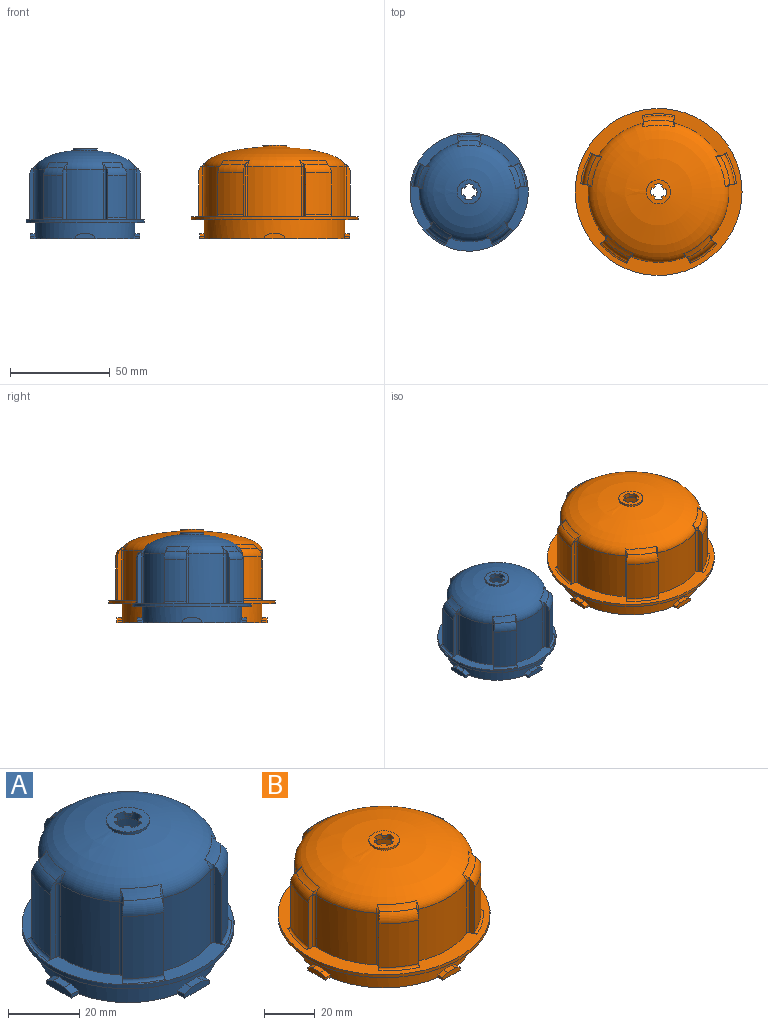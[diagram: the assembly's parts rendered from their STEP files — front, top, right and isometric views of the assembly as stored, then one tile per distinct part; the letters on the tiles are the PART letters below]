
ASSEMBLY  parts=2 mates=1
PART A: 108 faces, bbox 81.5x78.8x51.9 mm
  f0: revolved ~47x47mm, area 2029.6mm2, adj f4,f90
  f1: revolved ~50x50mm, area 2139.5mm2, adj f33,f37,f41,f45,f49,f52,f53,f54
  f2: plane 59.35x59.35mm, normal (0,0,1), area 574.8mm2, adj f30,f32,f33,f34,f36,f37,f38,f40
  f3: cylinder r=25mm len=50mm, axis (0,0,-1), area 1174.5mm2, adj f5,f7,f8,f9,f11,f12,f13,f15
  f4: cylinder r=23.5mm len=47mm, axis (0,0,-1), area 5079.3mm2, adj f0,f5
  f5: plane 54.75x54.75mm, normal (0,0,-1), area 328mm2, adj f3,f4,f6,f7,f8,f10,f11,f12
  f6: plane 9.8x2.4mm, normal (0,1,0), area 20.4mm2, adj f5,f7,f8,f9,f23,f27
  f7: plane 2.86x1.2mm, normal (-1,0,0), area 3.4mm2, adj f3,f5,f6,f23
  f8: plane 2.86x1.2mm, normal (1,0,0), area 3.4mm2, adj f3,f5,f6,f27
  f9: plane 4.6x2.48mm, normal (0,0,1), area 11.1mm2, adj f3,f6,f23,f27
  f10: plane 9.8x2.4mm, normal (1,0,0), area 20.4mm2, adj f5,f11,f12,f13,f24,f29
  f11: plane 2.86x1.2mm, normal (0,1,0), area 3.4mm2, adj f3,f5,f10,f24
  f12: plane 2.86x1.2mm, normal (0,-1,0), area 3.4mm2, adj f3,f5,f10,f29
  f13: plane 4.6x2.48mm, normal (0,0,1), area 11.1mm2, adj f3,f10,f24,f29
  f14: plane 9.8x2.4mm, normal (0,-1,0), area 20.4mm2, adj f5,f15,f16,f17,f25,f28
  f15: plane 2.86x1.2mm, normal (1,0,0), area 3.4mm2, adj f3,f5,f14,f25
  f16: plane 2.86x1.2mm, normal (-1,0,0), area 3.4mm2, adj f3,f5,f14,f28
  f17: plane 4.6x2.48mm, normal (0,0,1), area 11.1mm2, adj f3,f14,f25,f28
  f18: plane 9.8x2.4mm, normal (-1,0,0), area 20.4mm2, adj f5,f19,f20,f21,f22,f26
  f19: plane 2.86x1.2mm, normal (0,-1,0), area 3.4mm2, adj f3,f5,f18,f22
  f20: plane 2.86x1.2mm, normal (0,1,0), area 3.4mm2, adj f3,f5,f18,f26
  f21: plane 4.6x2.48mm, normal (0,0,1), area 11.1mm2, adj f3,f18,f22,f26
  f22: plane 2.86x2.6mm, normal (0,-0.42,0.91), area 7.6mm2, adj f3,f18,f19,f21
  f23: plane 2.86x2.6mm, normal (-0.42,0,0.91), area 7.6mm2, adj f3,f6,f7,f9
  f24: plane 2.86x2.6mm, normal (0,0.42,0.91), area 7.6mm2, adj f3,f10,f11,f13
  f25: plane 2.86x2.6mm, normal (0.42,0,0.91), area 7.6mm2, adj f3,f14,f15,f17
  f26: plane 2.86x2.6mm, normal (0,0.42,0.91), area 7.6mm2, adj f3,f18,f20,f21
  f27: plane 2.86x2.6mm, normal (0.42,0,0.91), area 7.6mm2, adj f3,f6,f8,f9
  f28: plane 2.86x2.6mm, normal (-0.42,0,0.91), area 7.6mm2, adj f3,f14,f16,f17
  f29: plane 2.86x2.6mm, normal (0,-0.42,0.91), area 7.6mm2, adj f3,f10,f12,f13
  f30: cylinder r=29.68mm len=59.35mm, axis (0,0,-1), area 261mm2, adj f2,f31
  f31: plane 59.35x59.35mm, normal (0,0,-1), area 803mm2, adj f3,f30
  f32: plane 26.45x3.16mm, normal (-0.98,-0.21,0), area 50.9mm2, adj f2,f51,f55,f61,f64,f65,f86
  f33: cylinder r=25mm len=25mm, axis (0,0,-1), area 475.5mm2, adj f1,f2,f64,f66
  f34: plane 26.45x2.8mm, normal (0.5,0.87,0), area 50.9mm2, adj f2,f35,f56,f60,f66,f67,f85
  f35: cylinder r=28mm len=21.27mm, axis (0,0,-1), area 249.5mm2, adj f34,f36,f60,f85
  f36: plane 26.45x3.21mm, normal (-0.1,-0.99,0), area 50.9mm2, adj f2,f35,f56,f60,f68,f69,f85
  f37: cylinder r=25mm len=25mm, axis (0,0,-1), area 475.5mm2, adj f1,f2,f68,f70
  f38: plane 26.45x2.4mm, normal (-0.67,0.74,0), area 50.9mm2, adj f2,f39,f52,f59,f70,f71,f84
  f39: cylinder r=28mm len=21.27mm, axis (0,0,-1), area 249.5mm2, adj f38,f40,f59,f84
  f40: plane 26.45x2.95mm, normal (0.91,-0.41,0), area 50.9mm2, adj f2,f39,f52,f59,f72,f73,f84
  f41: cylinder r=25mm len=25mm, axis (0,0,-1), area 475.5mm2, adj f1,f2,f72,f74
  f42: plane 26.45x2.95mm, normal (-0.91,-0.41,0), area 50.9mm2, adj f2,f43,f53,f58,f74,f75,f83
  f43: cylinder r=28mm len=21.27mm, axis (0,0,-1), area 249.5mm2, adj f42,f44,f58,f83
  f44: plane 26.45x2.4mm, normal (0.67,0.74,0), area 50.9mm2, adj f2,f43,f53,f58,f76,f77,f83
  f45: cylinder r=25mm len=25mm, axis (0,0,-1), area 475.5mm2, adj f1,f2,f76,f78
  f46: plane 26.45x3.21mm, normal (0.1,-0.99,0), area 50.9mm2, adj f2,f47,f54,f57,f78,f79,f82
  f47: cylinder r=28mm len=21.27mm, axis (0,0,-1), area 249.5mm2, adj f46,f48,f57,f82
  f48: plane 26.45x2.8mm, normal (-0.5,0.87,0), area 50.9mm2, adj f2,f47,f54,f57,f80,f81,f82
  f49: cylinder r=25mm len=25mm, axis (0,0,-1), area 475.5mm2, adj f1,f2,f62,f80
  f50: plane 26.45x3.16mm, normal (0.98,-0.21,0), area 50.9mm2, adj f2,f51,f55,f61,f62,f63,f86
  f51: cylinder r=28mm len=21.27mm, axis (0,0,-1), area 249.5mm2, adj f32,f50,f61,f86
  f52: torus R=37.73mm, axis (0,0,-1), area 38.3mm2, adj f1,f38,f40,f59,f71,f73
  f53: torus R=37.73mm, axis (0,0,-1), area 38.3mm2, adj f1,f42,f44,f58,f75,f77
  f54: torus R=37.73mm, axis (0,0,-1), area 38.3mm2, adj f1,f46,f48,f57,f79,f81
  f55: torus R=37.73mm, axis (0,0,-1), area 38.3mm2, adj f1,f32,f50,f61,f63,f65
  f56: torus R=37.73mm, axis (0,0,-1), area 38.3mm2, adj f1,f34,f36,f60,f67,f69
  f57: torus R=23mm, axis (0,0,1), area 53.8mm2, adj f46,f47,f48,f54
  f58: torus R=23mm, axis (0,0,1), area 53.8mm2, adj f42,f43,f44,f53
  f59: torus R=23mm, axis (0,0,1), area 53.8mm2, adj f38,f39,f40,f52
  f60: torus R=23mm, axis (0,0,1), area 53.8mm2, adj f34,f35,f36,f56
  f61: torus R=23mm, axis (0,0,1), area 53.8mm2, adj f32,f50,f51,f55
  f62: cylinder r=1mm len=25mm, axis (0,0,-1), area 38.3mm2, adj f2,f49,f50,f63
  f63: bspline ~6.12x3.69mm, area 4.2mm2, adj f1,f50,f55,f62
  f64: cylinder r=1mm len=25mm, axis (0,0,-1), area 38.3mm2, adj f2,f32,f33,f65
  f65: bspline ~6.12x3.69mm, area 4.2mm2, adj f1,f32,f55,f64
  f66: cylinder r=1mm len=25mm, axis (0,0,-1), area 38.3mm2, adj f2,f33,f34,f67
  f67: bspline ~6.12x3.57mm, area 4.2mm2, adj f1,f34,f56,f66
  f68: cylinder r=1mm len=25mm, axis (0,0,-1), area 38.3mm2, adj f2,f36,f37,f69
  f69: bspline ~6.12x3.53mm, area 4.2mm2, adj f1,f36,f56,f68
  f70: cylinder r=1mm len=25mm, axis (0,0,-1), area 38.3mm2, adj f2,f37,f38,f71
  f71: bspline ~6.12x3.11mm, area 4.2mm2, adj f1,f38,f52,f70
  f72: cylinder r=1mm len=25mm, axis (0,0,-1), area 38.3mm2, adj f2,f40,f41,f73
  f73: bspline ~6.12x3.24mm, area 4.2mm2, adj f1,f40,f52,f72
  f74: cylinder r=1mm len=25mm, axis (0,0,-1), area 38.3mm2, adj f2,f41,f42,f75
  f75: bspline ~6.12x3.24mm, area 4.2mm2, adj f1,f42,f53,f74
  f76: cylinder r=1mm len=25mm, axis (0,0,-1), area 38.3mm2, adj f2,f44,f45,f77
  f77: bspline ~6.12x3.11mm, area 4.2mm2, adj f1,f44,f53,f76
  f78: cylinder r=1mm len=25mm, axis (0,0,-1), area 38.3mm2, adj f2,f45,f46,f79
  f79: bspline ~6.12x3.53mm, area 4.2mm2, adj f1,f46,f54,f78
  f80: cylinder r=1mm len=25mm, axis (0,0,-1), area 38.3mm2, adj f2,f48,f49,f81
  f81: bspline ~6.12x3.57mm, area 4.2mm2, adj f1,f48,f54,f80
  f82: torus R=29mm, axis (0,0,1), area 18.7mm2, adj f2,f46,f47,f48
  f83: torus R=29mm, axis (0,0,1), area 18.7mm2, adj f2,f42,f43,f44
  f84: torus R=29mm, axis (0,0,1), area 18.7mm2, adj f2,f38,f39,f40
  f85: torus R=29mm, axis (0,0,1), area 18.7mm2, adj f2,f34,f35,f36
  f86: torus R=29mm, axis (0,0,1), area 18.7mm2, adj f2,f32,f50,f51
  f87: plane 12x12mm, normal (0,0,1), area 70.2mm2, adj f88,f89,f92,f93,f94,f96,f97,f98
  f88: cylinder r=6mm len=12mm, axis (0,0,-1), area 33.7mm2, adj f1,f87
  f89: cylinder r=4mm len=8mm, axis (0,0,-1), area 54.5mm2, adj f87,f91,f92,f94,f95,f96,f98,f99
  f90: cylinder r=6mm len=12mm, axis (0,0,-1), area 4.4mm2, adj f0,f91
  f91: plane 12x12mm, normal (0,0,-1), area 62.8mm2, adj f89,f90
  f92: plane 1x0.85mm, normal (-0.53,-0.85,0), area 1mm2, adj f87,f89,f93,f95
  f93: cylinder r=3mm len=1.14mm, axis (0,0,1), area 1.6mm2, adj f87,f92,f94,f95
  f94: plane 1x0.89mm, normal (0.89,0.47,0), area 1mm2, adj f87,f89,f93,f95
  f95: plane 1.99x1.94mm, normal (0,0,-1), area 1.8mm2, adj f89,f92,f93,f94
  f96: plane 1x0.85mm, normal (0.85,-0.53,0), area 1mm2, adj f87,f89,f97,f99
  f97: cylinder r=3mm len=1.14mm, axis (0,0,1), area 1.6mm2, adj f87,f96,f98,f99
  f98: plane 1x0.89mm, normal (-0.47,0.89,0), area 1mm2, adj f87,f89,f97,f99
  f99: plane 1.99x1.94mm, normal (0,0,-1), area 1.8mm2, adj f89,f96,f97,f98
  f100: plane 1x0.85mm, normal (0.53,0.85,0), area 1mm2, adj f87,f89,f101,f103
  f101: cylinder r=3mm len=1.14mm, axis (0,0,1), area 1.6mm2, adj f87,f100,f102,f103
  f102: plane 1x0.89mm, normal (-0.89,-0.47,0), area 1mm2, adj f87,f89,f101,f103
  f103: plane 1.99x1.94mm, normal (0,0,-1), area 1.8mm2, adj f89,f100,f101,f102
  f104: plane 1x0.85mm, normal (-0.85,0.53,0), area 1mm2, adj f87,f89,f105,f107
  f105: cylinder r=3mm len=1.14mm, axis (0,0,1), area 1.6mm2, adj f87,f104,f106,f107
  f106: plane 1x0.89mm, normal (0.47,-0.89,0), area 1mm2, adj f87,f89,f105,f107
  f107: plane 1.99x1.94mm, normal (0,0,-1), area 1.8mm2, adj f89,f104,f105,f106
PART B: 108 faces, bbox 100.9x97.4x46.7 mm
  f0: revolved ~67.5x67.5mm, area 3947.5mm2, adj f4,f90
  f1: revolved ~70.5x70.5mm, area 4124.4mm2, adj f33,f37,f41,f45,f49,f52,f53,f54
  f2: plane 83.68x83.68mm, normal (0,0,1), area 1282.3mm2, adj f30,f32,f33,f34,f36,f37,f38,f40
  f3: cylinder r=35.25mm len=70.5mm, axis (0,0,-1), area 2035.9mm2, adj f5,f7,f8,f9,f11,f12,f13,f15
  f4: cylinder r=33.75mm len=67.5mm, axis (0,0,-1), area 7625.9mm2, adj f0,f5
  f5: plane 75.25x75.25mm, normal (0,0,-1), area 422.7mm2, adj f3,f4,f6,f7,f8,f10,f11,f12
  f6: plane 9.8x2.4mm, normal (0,1,0), area 20.4mm2, adj f5,f7,f8,f9,f23,f27
  f7: plane 2.72x1.2mm, normal (-1,0,0), area 3.3mm2, adj f3,f5,f6,f23
  f8: plane 2.72x1.2mm, normal (1,0,0), area 3.3mm2, adj f3,f5,f6,f27
  f9: plane 4.6x2.45mm, normal (0,0,1), area 11mm2, adj f3,f6,f23,f27
  f10: plane 9.8x2.4mm, normal (1,0,0), area 20.4mm2, adj f5,f11,f12,f13,f24,f29
  f11: plane 2.72x1.2mm, normal (0,1,0), area 3.3mm2, adj f3,f5,f10,f24
  f12: plane 2.72x1.2mm, normal (0,-1,0), area 3.3mm2, adj f3,f5,f10,f29
  f13: plane 4.6x2.45mm, normal (0,0,1), area 11mm2, adj f3,f10,f24,f29
  f14: plane 9.8x2.4mm, normal (0,-1,0), area 20.4mm2, adj f5,f15,f16,f17,f25,f28
  f15: plane 2.72x1.2mm, normal (1,0,0), area 3.3mm2, adj f3,f5,f14,f25
  f16: plane 2.72x1.2mm, normal (-1,0,0), area 3.3mm2, adj f3,f5,f14,f28
  f17: plane 4.6x2.45mm, normal (0,0,1), area 11mm2, adj f3,f14,f25,f28
  f18: plane 9.8x2.4mm, normal (-1,0,0), area 20.4mm2, adj f5,f19,f20,f21,f22,f26
  f19: plane 2.72x1.2mm, normal (0,-1,0), area 3.3mm2, adj f3,f5,f18,f22
  f20: plane 2.72x1.2mm, normal (0,1,0), area 3.3mm2, adj f3,f5,f18,f26
  f21: plane 4.6x2.45mm, normal (0,0,1), area 11mm2, adj f3,f18,f22,f26
  f22: plane 2.72x2.6mm, normal (0,-0.42,0.91), area 7.4mm2, adj f3,f18,f19,f21
  f23: plane 2.72x2.6mm, normal (-0.42,0,0.91), area 7.4mm2, adj f3,f6,f7,f9
  f24: plane 2.72x2.6mm, normal (0,0.42,0.91), area 7.4mm2, adj f3,f10,f11,f13
  f25: plane 2.72x2.6mm, normal (0.42,0,0.91), area 7.4mm2, adj f3,f14,f15,f17
  f26: plane 2.72x2.6mm, normal (0,0.42,0.91), area 7.4mm2, adj f3,f18,f20,f21
  f27: plane 2.72x2.6mm, normal (0.42,0,0.91), area 7.4mm2, adj f3,f6,f8,f9
  f28: plane 2.72x2.6mm, normal (-0.42,0,0.91), area 7.4mm2, adj f3,f14,f16,f17
  f29: plane 2.72x2.6mm, normal (0,-0.42,0.91), area 7.4mm2, adj f3,f10,f12,f13
  f30: cylinder r=41.84mm len=83.68mm, axis (0,0,-1), area 368.1mm2, adj f2,f31
  f31: plane 83.68x83.68mm, normal (0,0,-1), area 1596.5mm2, adj f3,f30
  f32: plane 26.21x3.14mm, normal (-0.98,-0.21,0), area 50.3mm2, adj f2,f51,f61,f64,f65,f86
  f33: cylinder r=35.25mm len=25mm, axis (0,0,-1), area 689.6mm2, adj f1,f2,f64,f66
  f34: plane 26.21x2.78mm, normal (0.5,0.87,0), area 50.3mm2, adj f2,f35,f60,f66,f67,f85
  f35: cylinder r=38.25mm len=21.06mm, axis (0,0,-1), area 337.4mm2, adj f34,f36,f60,f85
  f36: plane 26.21x3.19mm, normal (-0.1,-0.99,0), area 50.3mm2, adj f2,f35,f60,f68,f69,f85
  f37: cylinder r=35.25mm len=25.57mm, axis (0,0,-1), area 689.6mm2, adj f1,f2,f68,f70
  f38: plane 26.21x2.38mm, normal (-0.67,0.74,0), area 50.3mm2, adj f2,f39,f59,f70,f71,f84
  f39: cylinder r=38.25mm len=21.06mm, axis (0,0,-1), area 337.4mm2, adj f38,f40,f59,f84
  f40: plane 26.21x2.93mm, normal (0.91,-0.41,0), area 50.3mm2, adj f2,f39,f59,f72,f73,f84
  f41: cylinder r=35.25mm len=26.89mm, axis (0,0,-1), area 689.6mm2, adj f1,f2,f72,f74
  f42: plane 26.21x2.93mm, normal (-0.91,-0.41,0), area 50.3mm2, adj f2,f43,f58,f74,f75,f83
  f43: cylinder r=38.25mm len=21.06mm, axis (0,0,-1), area 337.4mm2, adj f42,f44,f58,f83
  f44: plane 26.21x2.38mm, normal (0.67,0.74,0), area 50.3mm2, adj f2,f43,f58,f76,f77,f83
  f45: cylinder r=35.25mm len=25.57mm, axis (0,0,-1), area 689.6mm2, adj f1,f2,f76,f78
  f46: plane 26.21x3.19mm, normal (0.1,-0.99,0), area 50.3mm2, adj f2,f47,f57,f78,f79,f82
  f47: cylinder r=38.25mm len=21.06mm, axis (0,0,-1), area 337.4mm2, adj f46,f48,f57,f82
  f48: plane 26.21x2.78mm, normal (-0.5,0.87,0), area 50.3mm2, adj f2,f47,f57,f80,f81,f82
  f49: cylinder r=35.25mm len=25mm, axis (0,0,-1), area 689.6mm2, adj f1,f2,f62,f80
  f50: plane 26.21x3.14mm, normal (0.98,-0.21,0), area 50.3mm2, adj f2,f51,f61,f62,f63,f86
  f51: cylinder r=38.25mm len=21.06mm, axis (0,0,-1), area 337.4mm2, adj f32,f50,f61,f86
  f52: torus R=46.72mm, axis (0,0,-1), area 46.9mm2, adj f1,f59,f71,f73
  f53: torus R=46.72mm, axis (0,0,-1), area 46.9mm2, adj f1,f58,f75,f77
  f54: torus R=46.72mm, axis (0,0,-1), area 46.9mm2, adj f1,f57,f79,f81
  f55: torus R=46.72mm, axis (0,0,-1), area 46.9mm2, adj f1,f61,f63,f65
  f56: torus R=46.72mm, axis (0,0,-1), area 46.9mm2, adj f1,f60,f67,f69
  f57: torus R=33.25mm, axis (0,0,1), area 78.6mm2, adj f46,f47,f48,f54,f79,f81
  f58: torus R=33.25mm, axis (0,0,1), area 78.6mm2, adj f42,f43,f44,f53,f75,f77
  f59: torus R=33.25mm, axis (0,0,1), area 78.6mm2, adj f38,f39,f40,f52,f71,f73
  f60: torus R=33.25mm, axis (0,0,1), area 78.6mm2, adj f34,f35,f36,f56,f67,f69
  f61: torus R=33.25mm, axis (0,0,1), area 78.6mm2, adj f32,f50,f51,f55,f63,f65
  f62: cylinder r=1mm len=25mm, axis (0,0,-1), area 38.6mm2, adj f2,f49,f50,f63
  f63: bspline ~4.73x3.44mm, area 3.4mm2, adj f1,f50,f55,f61,f62
  f64: cylinder r=1mm len=25mm, axis (0,0,-1), area 38.6mm2, adj f2,f32,f33,f65
  f65: bspline ~4.73x3.44mm, area 3.4mm2, adj f1,f32,f55,f61,f64
  f66: cylinder r=1mm len=25mm, axis (0,0,-1), area 38.6mm2, adj f2,f33,f34,f67
  f67: bspline ~4.73x3.36mm, area 3.4mm2, adj f1,f34,f56,f60,f66
  f68: cylinder r=1mm len=25mm, axis (0,0,-1), area 38.6mm2, adj f2,f36,f37,f69
  f69: bspline ~4.73x3.28mm, area 3.4mm2, adj f1,f36,f56,f60,f68
  f70: cylinder r=1mm len=25mm, axis (0,0,-1), area 38.6mm2, adj f2,f37,f38,f71
  f71: bspline ~4.73x2.95mm, area 3.4mm2, adj f1,f38,f52,f59,f70
  f72: cylinder r=1mm len=25mm, axis (0,0,-1), area 38.6mm2, adj f2,f40,f41,f73
  f73: bspline ~4.73x3.02mm, area 3.4mm2, adj f1,f40,f52,f59,f72
  f74: cylinder r=1mm len=25mm, axis (0,0,-1), area 38.6mm2, adj f2,f41,f42,f75
  f75: bspline ~4.73x3.02mm, area 3.4mm2, adj f1,f42,f53,f58,f74
  f76: cylinder r=1mm len=25mm, axis (0,0,-1), area 38.6mm2, adj f2,f44,f45,f77
  f77: bspline ~4.73x2.95mm, area 3.4mm2, adj f1,f44,f53,f58,f76
  f78: cylinder r=1mm len=25mm, axis (0,0,-1), area 38.6mm2, adj f2,f45,f46,f79
  f79: bspline ~4.73x3.28mm, area 3.4mm2, adj f1,f46,f54,f57,f78
  f80: cylinder r=1mm len=25mm, axis (0,0,-1), area 38.6mm2, adj f2,f48,f49,f81
  f81: bspline ~4.73x3.36mm, area 3.4mm2, adj f1,f48,f54,f57,f80
  f82: torus R=39.25mm, axis (0,0,1), area 25.4mm2, adj f2,f46,f47,f48
  f83: torus R=39.25mm, axis (0,0,1), area 25.4mm2, adj f2,f42,f43,f44
  f84: torus R=39.25mm, axis (0,0,1), area 25.4mm2, adj f2,f38,f39,f40
  f85: torus R=39.25mm, axis (0,0,1), area 25.4mm2, adj f2,f34,f35,f36
  f86: torus R=39.25mm, axis (0,0,1), area 25.4mm2, adj f2,f32,f50,f51
  f87: plane 12x12mm, normal (0,0,1), area 70.2mm2, adj f88,f89,f92,f93,f94,f96,f97,f98
  f88: cylinder r=6mm len=12mm, axis (0,0,-1), area 33.3mm2, adj f1,f87
  f89: cylinder r=4mm len=8mm, axis (0,0,-1), area 54.5mm2, adj f87,f91,f92,f94,f95,f96,f98,f99
  f90: cylinder r=6mm len=12mm, axis (0,0,-1), area 4.8mm2, adj f0,f91
  f91: plane 12x12mm, normal (0,0,-1), area 62.8mm2, adj f89,f90
  f92: plane 1x0.85mm, normal (-0.53,-0.85,0), area 1mm2, adj f87,f89,f93,f95
  f93: cylinder r=3mm len=1.14mm, axis (0,0,1), area 1.6mm2, adj f87,f92,f94,f95
  f94: plane 1x0.89mm, normal (0.89,0.47,0), area 1mm2, adj f87,f89,f93,f95
  f95: plane 1.99x1.94mm, normal (0,0,-1), area 1.8mm2, adj f89,f92,f93,f94
  f96: plane 1x0.85mm, normal (0.85,-0.53,0), area 1mm2, adj f87,f89,f97,f99
  f97: cylinder r=3mm len=1.14mm, axis (0,0,1), area 1.6mm2, adj f87,f96,f98,f99
  f98: plane 1x0.89mm, normal (-0.47,0.89,0), area 1mm2, adj f87,f89,f97,f99
  f99: plane 1.99x1.94mm, normal (0,0,-1), area 1.8mm2, adj f89,f96,f97,f98
  f100: plane 1x0.85mm, normal (0.53,0.85,0), area 1mm2, adj f87,f89,f101,f103
  f101: cylinder r=3mm len=1.14mm, axis (0,0,1), area 1.6mm2, adj f87,f100,f102,f103
  f102: plane 1x0.89mm, normal (-0.89,-0.47,0), area 1mm2, adj f87,f89,f101,f103
  f103: plane 1.99x1.94mm, normal (0,0,-1), area 1.8mm2, adj f89,f100,f101,f102
  f104: plane 1x0.85mm, normal (-0.85,0.53,0), area 1mm2, adj f87,f89,f105,f107
  f105: cylinder r=3mm len=1.14mm, axis (0,0,1), area 1.6mm2, adj f87,f104,f106,f107
  f106: plane 1x0.89mm, normal (0.47,-0.89,0), area 1mm2, adj f87,f89,f105,f107
  f107: plane 1.99x1.94mm, normal (0,0,-1), area 1.8mm2, adj f89,f104,f105,f106
PLACE A at identity
PLACE B t=(95,0,0)mm
MATE fastened A.f5 <-> B.f5  axis (0,0,-1) through (27.38,0,0)mm
